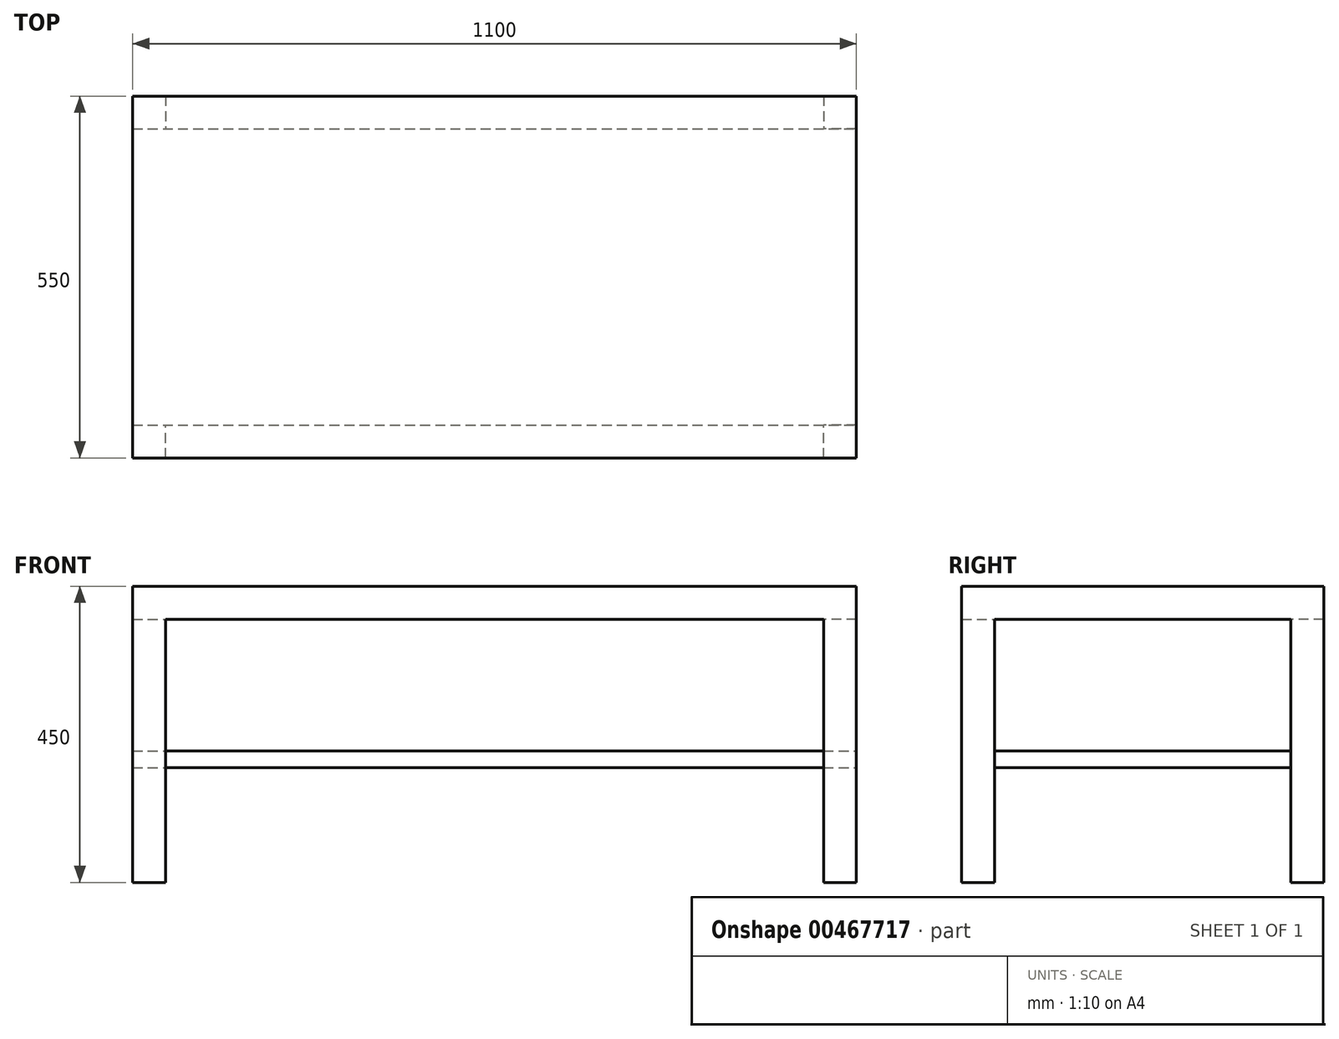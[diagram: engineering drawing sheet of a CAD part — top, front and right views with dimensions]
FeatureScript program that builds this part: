
annotation { "Feature Type Name" : "Feature", "Feature Type Description" : "" }
export const myFeature = defineFeature(function(context is Context, id is Id, definition is map)
    precondition{}
    {
        {
            var Q0;
            Q0=qCreatedBy(makeId("Top.planeOp"),FACE);
            var sketch = newSketch(context, id + "F0", { "sketchPlane" : qUnion([Q0])});
            skLineSegment(sketch, "E0.bottom", {"start": v(550, 275) * mm, "end": v(-550, 275) * mm});
            skLineSegment(sketch, "E0.top", {"start": v(550, -275) * mm, "end": v(-550, -275) * mm});
            skLineSegment(sketch, "E0.left", {"start": v(550, 275) * mm, "end": v(550, -275) * mm});
            skLineSegment(sketch, "E0.right", {"start": v(-550, 275) * mm, "end": v(-550, -275) * mm});
            skPoint(sketch, "E0.middle", {"position": v(0, 0) * mm});
            skSolve(sketch);
        }
        {
            var Q0;
            Q0 = qSketchRegion(id + "F0", true);
            extrude(context, id + "F1", {"entities" : qUnion([Q0]), "depth" : 50 * mm});
        }
        {
            var Q0;
            Q0=makeQuery(id+"F1.opExtrude","CAP_FACE",FACE,{"disambiguationData":[OSD([sQuery(id+"F0.wireOp",EDGE,"E0.bottom"),sQuery(id+"F0.wireOp",EDGE,"E0.top"),sQuery(id+"F0.wireOp",EDGE,"E0.left"),sQuery(id+"F0.wireOp",EDGE,"E0.right")])],"isStart":true});
            var sketch = newSketch(context, id + "F2", { "sketchPlane" : qUnion([Q0])});
            skLineSegment(sketch, "E1.bottom", {"start": v(-550, 275) * mm, "end": v(-500, 275) * mm});
            skLineSegment(sketch, "E1.top", {"start": v(-550, 225) * mm, "end": v(-500, 225) * mm});
            skLineSegment(sketch, "E1.left", {"start": v(-550, 275) * mm, "end": v(-550, 225) * mm});
            skLineSegment(sketch, "E1.right", {"start": v(-500, 275) * mm, "end": v(-500, 225) * mm});
            skLineSegment(sketch, "E2.bottom", {"start": v(-550, -275) * mm, "end": v(-500, -275) * mm});
            skLineSegment(sketch, "E2.top", {"start": v(-550, -225) * mm, "end": v(-500, -225) * mm});
            skLineSegment(sketch, "E2.left", {"start": v(-550, -275) * mm, "end": v(-550, -225) * mm});
            skLineSegment(sketch, "E2.right", {"start": v(-500, -275) * mm, "end": v(-500, -225) * mm});
            skLineSegment(sketch, "E3.bottom", {"start": v(550, -275) * mm, "end": v(500, -275) * mm});
            skLineSegment(sketch, "E3.top", {"start": v(550, -225) * mm, "end": v(500, -225) * mm});
            skLineSegment(sketch, "E3.left", {"start": v(550, -275) * mm, "end": v(550, -225) * mm});
            skLineSegment(sketch, "E3.right", {"start": v(500, -275) * mm, "end": v(500, -225) * mm});
            skLineSegment(sketch, "E4.bottom", {"start": v(550, 275) * mm, "end": v(500, 275) * mm});
            skLineSegment(sketch, "E4.top", {"start": v(550, 225) * mm, "end": v(500, 225) * mm});
            skLineSegment(sketch, "E4.left", {"start": v(550, 275) * mm, "end": v(550, 225) * mm});
            skLineSegment(sketch, "E4.right", {"start": v(500, 275) * mm, "end": v(500, 225) * mm});
            skSolve(sketch);
        }
        {
            var Q0;
            Q0 = qSketchRegion(id + "F2", true);
            extrude(context, id + "F3", {"entities" : qUnion([Q0]), "operationType" : NewBodyOperationType.ADD, "depth" : 400 * mm});
        }
        {
            var Q0;
            Q0=makeQuery(id+"F1.opExtrude","CAP_FACE",FACE,{"disambiguationData":[OSD([sQuery(id+"F0.wireOp",EDGE,"E0.bottom"),sQuery(id+"F0.wireOp",EDGE,"E0.top"),sQuery(id+"F0.wireOp",EDGE,"E0.left"),sQuery(id+"F0.wireOp",EDGE,"E0.right")])],"isStart":true});
            cPlane(context, id + "F4", {"entities" : qUnion([Q0]), "cplaneType" : CPlaneType.OFFSET, "offset" : 200 * mm, "width" : 152.4 * mm, "height" : 152.4 * mm});
        }
        {
            var Q0;
            Q0=qCreatedBy(id+"F4.planeOp",FACE);
            var sketch = newSketch(context, id + "F5", { "sketchPlane" : qUnion([Q0])});
            skLineSegment(sketch, "E5.bottom", {"start": v(-550, 225) * mm, "end": v(550, 225) * mm});
            skLineSegment(sketch, "E5.top", {"start": v(-550, -225) * mm, "end": v(550, -225) * mm});
            skLineSegment(sketch, "E5.left", {"start": v(-550, 225) * mm, "end": v(-550, -225) * mm});
            skLineSegment(sketch, "E5.right", {"start": v(550, 225) * mm, "end": v(550, -225) * mm});
            skPoint(sketch, "E5.middle", {"position": v(0, 0) * mm});
            skSolve(sketch);
        }
        {
            var Q0;
            Q0=makeQuery(id+"F5.imprint","IMPRINT",FACE,{"disambiguationData":[TD([[makeQuery(id+"F5.imprint","IMPRINT",EDGE,{"derivedFrom":sQuery(id+"F5.wireOp",EDGE,"E5.bottom")}),-1.0]])]});
            extrude(context, id + "F6", {"entities" : qUnion([Q0]), "depth" : 25.4 * mm});
        }
    });
